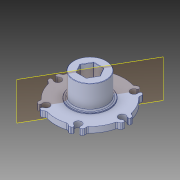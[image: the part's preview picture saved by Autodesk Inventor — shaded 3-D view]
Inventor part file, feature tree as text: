
AUTODESK INVENTOR PART (.ipt)
format: ipt  version: 2016 SP1 (Build 200210100, 210)  size: 325,632 bytes
history: native  units: in
note: dims shown in document units (in); Inventor stores cm internally (conversion verified against a paired STEP export)
features: plane x1, fillet x1
ambient origin geometry x8: Origin, YZ Plane, XZ Plane, XY Plane, X Axis, Y Axis, Z Axis, Center Point
bodies: Solid1 (feature_tree)
feature tree (2):
  plane  "Work Plane1"
  fillet  "Fillet7"  [1 undecoded]
note: 1 required parameter value undecoded (feature->parameter linkage not recoverable at this tier; creation-order binding heuristic only, values carry confidence <= 0.55)
